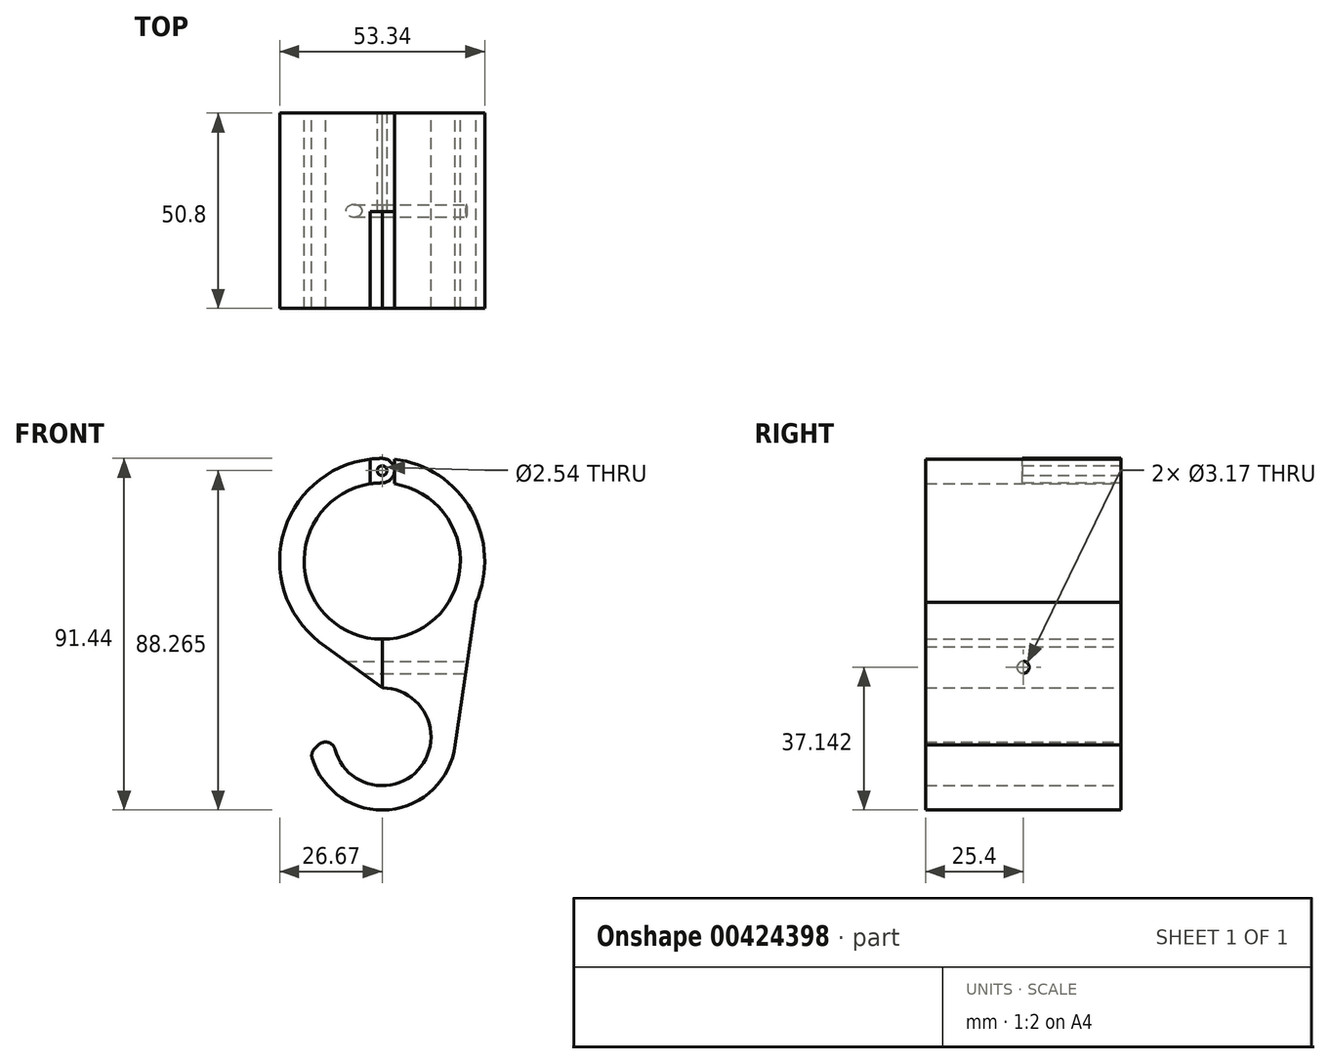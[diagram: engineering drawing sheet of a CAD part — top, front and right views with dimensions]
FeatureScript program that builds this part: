
annotation { "Feature Type Name" : "Feature", "Feature Type Description" : "" }
export const myFeature = defineFeature(function(context is Context, id is Id, definition is map)
    precondition{}
    {
        {
            var Q0;
            Q0=qCreatedBy(makeId("Front.planeOp"),FACE);
            var sketch = newSketch(context, id + "F0", { "sketchPlane" : qUnion([Q0])});
            skCircle(sketch, "E0", {"center": v(0, 0) * mm, "radius": 19.05 * mm, "construction": true});
            skCircle(sketch, "E1", {"center": v(0, 0) * mm, "radius": 20.32 * mm, "construction": true});
            skCircle(sketch, "E2", {"center": v(0, 0) * mm, "radius": 26.67 * mm, "construction": true});
            skArc(sketch, "E3", {"start": v(-18.63, -49.7) * mm, "mid": v(14.81, -57.7) * mm, "end": v(0, -26.67) * mm});
            skArc(sketch, "E4", {"start": v(-12.62, -44.33) * mm, "mid": v(8.47, -55.18) * mm, "end": v(0, -33.02) * mm});
            skLineSegment(sketch, "E5", {"start": v(-18.63, -49.7) * mm, "end": v(-12.62, -44.33) * mm});
            skLineSegment(sketch, "E6", {"start": v(0, -26.67) * mm, "end": v(0, -33.02) * mm});
            skLineSegment(sketch, "E7", {"start": v(18.74, -49.15) * mm, "end": v(24.4, -10.75) * mm});
            skLineSegment(sketch, "E8", {"start": v(-14.73, -22.24) * mm, "end": v(0, -33.02) * mm});
            skLineSegment(sketch, "E9", {"start": v(-3.17, 26.48) * mm, "end": v(-3.17, 20.07) * mm});
            skLineSegment(sketch, "E10", {"start": v(0, -20.32) * mm, "end": v(0, -26.67) * mm});
            skArc(sketch, "E11", {"start": v(-3.17, 20.07) * mm, "mid": v(20.26, 1.6) * mm, "end": v(0, -20.32) * mm});
            skArc(sketch, "E12", {"start": v(-3.18, 26.48) * mm, "mid": v(26.62, 1.6) * mm, "end": v(0, -26.67) * mm});
            skLineSegment(sketch, "E13", {"start": v(0, 26.67) * mm, "end": v(0, 20.32) * mm, "construction": true});
            skCircle(sketch, "E14", {"center": v(0, 23.5) * mm, "radius": 1.27 * mm});
            skSolve(sketch);
        }
        {
            var Q0;
            Q0 = qSketchRegion(id + "F0", true);
            extrude(context, id + "F1", {"entities" : qUnion([Q0]), "depth" : 76.2 * mm});
        }
        {
            var Q0;
            Q0=qCreatedBy(makeId("Top.planeOp"),FACE);
            cPlane(context, id + "F2", {"entities" : qUnion([Q0]), "cplaneType" : CPlaneType.OFFSET, "offset" : 101.6 * mm, "width" : 152.4 * mm, "height" : 152.4 * mm});
        }
        {
            var Q0;
            Q0=qCreatedBy(id+"F2.planeOp",FACE);
            var sketch = newSketch(context, id + "F3", { "sketchPlane" : qUnion([Q0])});
            skLineSegment(sketch, "E15.bottom", {"start": v(-3.17, 0) * mm, "end": v(3.17, 0) * mm});
            skLineSegment(sketch, "E15.top", {"start": v(-3.17, -38.3) * mm, "end": v(3.18, -38.3) * mm});
            skLineSegment(sketch, "E15.left", {"start": v(-3.17, 0) * mm, "end": v(-3.17, -38.3) * mm});
            skLineSegment(sketch, "E15.right", {"start": v(3.17, 0) * mm, "end": v(3.18, -38.3) * mm});
            skSolve(sketch);
        }
        {
            var Q0;
            Q0 = qSketchRegion(id + "F3", true);
            extrude(context, id + "F4", {"entities" : qUnion([Q0]), "operationType" : NewBodyOperationType.REMOVE, "oppositeDirection" : true, "depth" : 88.65 * mm});
        }
        {
            var Q0;
            Q0=qCreatedBy(makeId("Front.planeOp"),FACE);
            var sketch = newSketch(context, id + "F5", { "sketchPlane" : qUnion([Q0])});
            skArc(sketch, "E16", {"start": v(5.42, 19.58) * mm, "mid": v(-20.13, 2.74) * mm, "end": v(0, -20.32) * mm});
            skArc(sketch, "E17", {"start": v(3.17, 26.48) * mm, "mid": v(-26.62, 1.6) * mm, "end": v(0, -26.67) * mm});
            skLineSegment(sketch, "E18.0", {"start": v(3.17, 20.07) * mm, "end": v(3.17, 26.48) * mm});
            skLineSegment(sketch, "E19.0", {"start": v(0, -20.32) * mm, "end": v(0, -26.67) * mm});
            skCircle(sketch, "E20.0", {"center": v(0, 23.5) * mm, "radius": 1.27 * mm});
            skLineSegment(sketch, "E21.0", {"start": v(-14.73, -22.24) * mm, "end": v(0, -33.02) * mm});
            skLineSegment(sketch, "E22.0", {"start": v(0, -26.67) * mm, "end": v(0, -33.02) * mm});
            skSolve(sketch);
        }
        {
            var Q0;
            Q0 = qSketchRegion(id + "F5", true);
            extrude(context, id + "F6", {"entities" : qUnion([Q0]), "depth" : 76.2 * mm});
        }
        {
            var Q0;
            Q0=qCreatedBy(id+"F2.planeOp",FACE);
            var sketch = newSketch(context, id + "F7", { "sketchPlane" : qUnion([Q0])});
            skLineSegment(sketch, "E23.0", {"start": v(-3.17, -38.3) * mm, "end": v(3.18, -38.3) * mm});
            skLineSegment(sketch, "E24.0", {"start": v(-3.17, -76.2) * mm, "end": v(3.18, -76.2) * mm});
            skLineSegment(sketch, "E25", {"start": v(-3.17, -38.3) * mm, "end": v(-3.17, -76.2) * mm});
            skLineSegment(sketch, "E26", {"start": v(3.18, -38.3) * mm, "end": v(3.18, -76.2) * mm});
            skPoint(sketch, "E27.orphan", {"position": v(-3.17, -76.2) * mm});
            skPoint(sketch, "E28.orphan", {"position": v(26.67, -76.2) * mm});
            skSolve(sketch);
        }
        {
            var Q0;
            Q0 = qSketchRegion(id + "F7", true);
            extrude(context, id + "F8", {"entities" : qUnion([Q0]), "operationType" : NewBodyOperationType.REMOVE, "oppositeDirection" : true, "depth" : 98.8 * mm});
        }
        {
            var Q0;
            Q0=qCreatedBy(makeId("Right.planeOp"),FACE);
            cPlane(context, id + "F9", {"entities" : qUnion([Q0]), "cplaneType" : CPlaneType.OFFSET, "offset" : 76.2 * mm, "width" : 152.4 * mm, "height" : 152.4 * mm});
        }
        {
            var Q0;
            Q0=qCreatedBy(id+"F9.planeOp",FACE);
            var sketch = newSketch(context, id + "F10", { "sketchPlane" : qUnion([Q0])});
            skLineSegment(sketch, "E29.0", {"start": v(-76.2, -22.24) * mm, "end": v(0, -22.24) * mm, "construction": true});
            skLineSegment(sketch, "E30.0", {"start": v(-76.2, -33.02) * mm, "end": v(0, -33.02) * mm, "construction": true});
            skLineSegment(sketch, "E31", {"start": v(-38.1, -22.24) * mm, "end": v(-38.1, -33.02) * mm});
            skCircle(sketch, "E32", {"center": v(-38.1, -27.63) * mm, "radius": 1.59 * mm});
            skSolve(sketch);
        }
        {
            var Q0;
            Q0 = qSketchRegion(id + "F10", true);
            extrude(context, id + "F11", {"entities" : qUnion([Q0]), "operationType" : NewBodyOperationType.REMOVE, "oppositeDirection" : true, "depth" : 145.54 * mm});
        }
        {
            var Q0;
            Q0=makeQuery(id+"F1.opExtrude","SWEPT_EDGE",EDGE,{"disambiguationData":[OSD([sQuery(id+"F0.wireOp",EDGE,"E4"),sQuery(id+"F0.wireOp",EDGE,"E5")])]});
            var Q1;
            Q1=makeQuery(id+"F1.opExtrude","SWEPT_EDGE",EDGE,{"disambiguationData":[OSD([sQuery(id+"F0.wireOp",EDGE,"E3"),sQuery(id+"F0.wireOp",EDGE,"E5")])]});
            fillet(context, id + "F12", {"entities" : qUnion([Q0, Q1]), "radius" : 2.54 * mm, "tangentPropagation" : true, "allowEdgeOverflow" : false});
        }
        {
            var Q0;
            Q0=makeQuery(id+"F1.opExtrude","SWEPT_EDGE",EDGE,{"disambiguationData":[OSD([sQuery(id+"F0.wireOp",EDGE,"E9"),sQuery(id+"F0.wireOp",EDGE,"E12")])]});
            var Q1;
            Q1=makeQuery(id+"F1.opExtrude","SWEPT_EDGE",EDGE,{"disambiguationData":[OSD([sQuery(id+"F0.wireOp",EDGE,"E9"),sQuery(id+"F0.wireOp",EDGE,"E11")])]});
            var Q2;
            Q2=makeQuery(id+"F6.opExtrude","SWEPT_EDGE",EDGE,{"disambiguationData":[OSD([sQuery(id+"F5.wireOp",EDGE,"E17"),sQuery(id+"F5.wireOp",EDGE,"E18.0")])]});
            var Q3;
            Q3=makeQuery(id+"F6.opExtrude","SWEPT_EDGE",EDGE,{"disambiguationData":[OSD([sQuery(id+"F5.wireOp",EDGE,"E16"),sQuery(id+"F5.wireOp",EDGE,"E18.0")])]});
            fillet(context, id + "F13", {"entities" : qUnion([Q0, Q1, Q2, Q3]), "radius" : 3.17 * mm, "tangentPropagation" : true, "allowEdgeOverflow" : false});
        }
        {
            var Q0;
            Q0=qCreatedBy(makeId("Right.planeOp"),FACE);
            var sketch = newSketch(context, id + "F14", { "sketchPlane" : qUnion([Q0])});
            skLineSegment(sketch, "E33.bottom", {"start": v(0, 54.3) * mm, "end": v(-12.7, 54.3) * mm});
            skLineSegment(sketch, "E33.top", {"start": v(0, -83.81) * mm, "end": v(-12.7, -83.81) * mm});
            skLineSegment(sketch, "E33.left", {"start": v(0, 54.3) * mm, "end": v(0, -83.81) * mm});
            skLineSegment(sketch, "E33.right", {"start": v(-12.7, 54.3) * mm, "end": v(-12.7, -83.81) * mm});
            skLineSegment(sketch, "E34.bottom", {"start": v(-76.2, 53.82) * mm, "end": v(-63.5, 53.82) * mm});
            skLineSegment(sketch, "E34.top", {"start": v(-76.2, -83.97) * mm, "end": v(-63.5, -83.97) * mm});
            skLineSegment(sketch, "E34.left", {"start": v(-76.2, 53.82) * mm, "end": v(-76.2, -83.97) * mm});
            skLineSegment(sketch, "E34.right", {"start": v(-63.5, 53.82) * mm, "end": v(-63.5, -83.97) * mm});
            skSolve(sketch);
        }
        {
            var Q0;
            Q0 = qSketchRegion(id + "F14", true);
            extrude(context, id + "F15", {"entities" : qUnion([Q0]), "operationType" : NewBodyOperationType.REMOVE, "depth" : 127 * mm, "hasSecondDirection" : true, "secondDirectionOppositeDirection" : true, "secondDirectionDepth" : 127 * mm});
        }
    });
